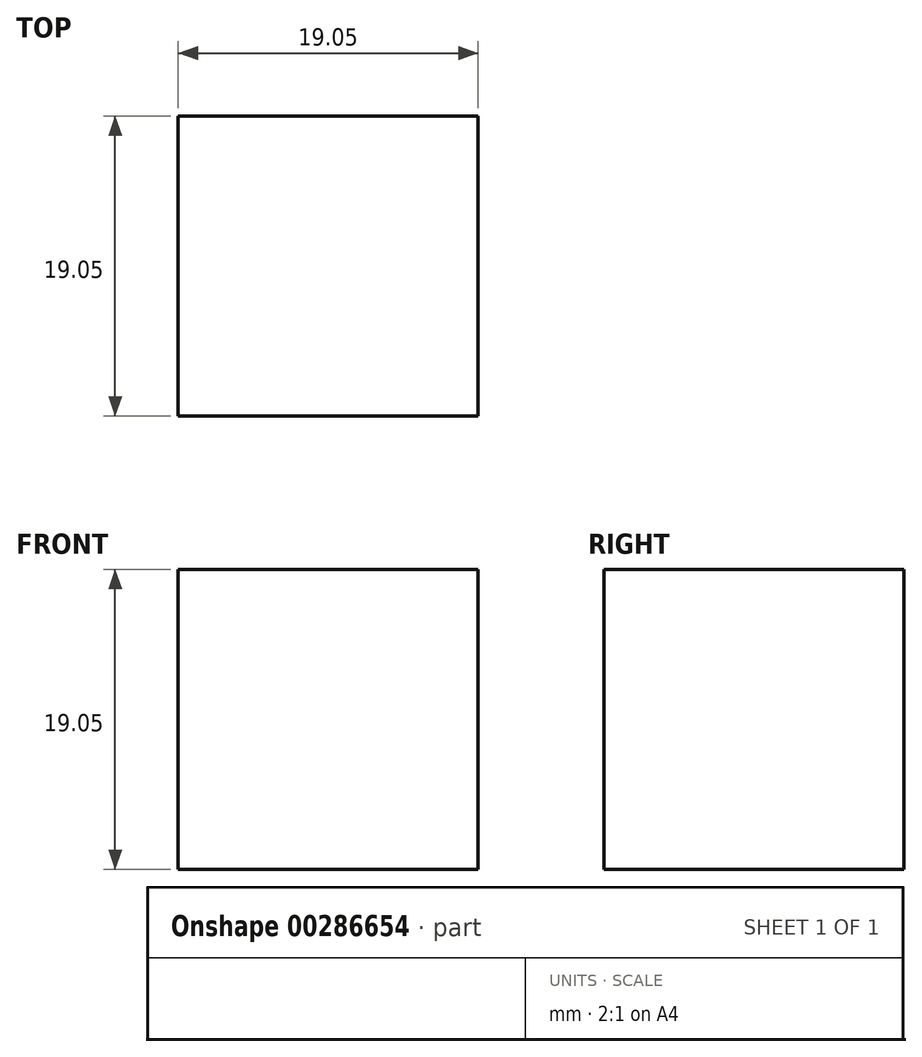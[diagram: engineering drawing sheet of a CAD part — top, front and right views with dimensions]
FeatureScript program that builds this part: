
annotation { "Feature Type Name" : "Feature", "Feature Type Description" : "" }
export const myFeature = defineFeature(function(context is Context, id is Id, definition is map)
    precondition{}
    {
        {
            var Q0;
            Q0=qCreatedBy(makeId("Front.planeOp"),FACE);
            var sketch = newSketch(context, id + "F0", { "sketchPlane" : qUnion([Q0])});
            skLineSegment(sketch, "E0.bottom", {"start": v(-41.22, 51.3) * mm, "end": v(-22.17, 51.3) * mm});
            skLineSegment(sketch, "E0.top", {"start": v(-41.22, 32.26) * mm, "end": v(-22.17, 32.26) * mm});
            skLineSegment(sketch, "E0.left", {"start": v(-41.22, 51.3) * mm, "end": v(-41.22, 32.26) * mm});
            skLineSegment(sketch, "E0.right", {"start": v(-22.17, 51.3) * mm, "end": v(-22.17, 32.26) * mm});
            skSolve(sketch);
        }
        {
            var Q0;
            Q0 = qSketchRegion(id + "F0", true);
            extrude(context, id + "F1", {"entities" : qUnion([Q0]), "depth" : 19.05 * mm});
        }
    });
